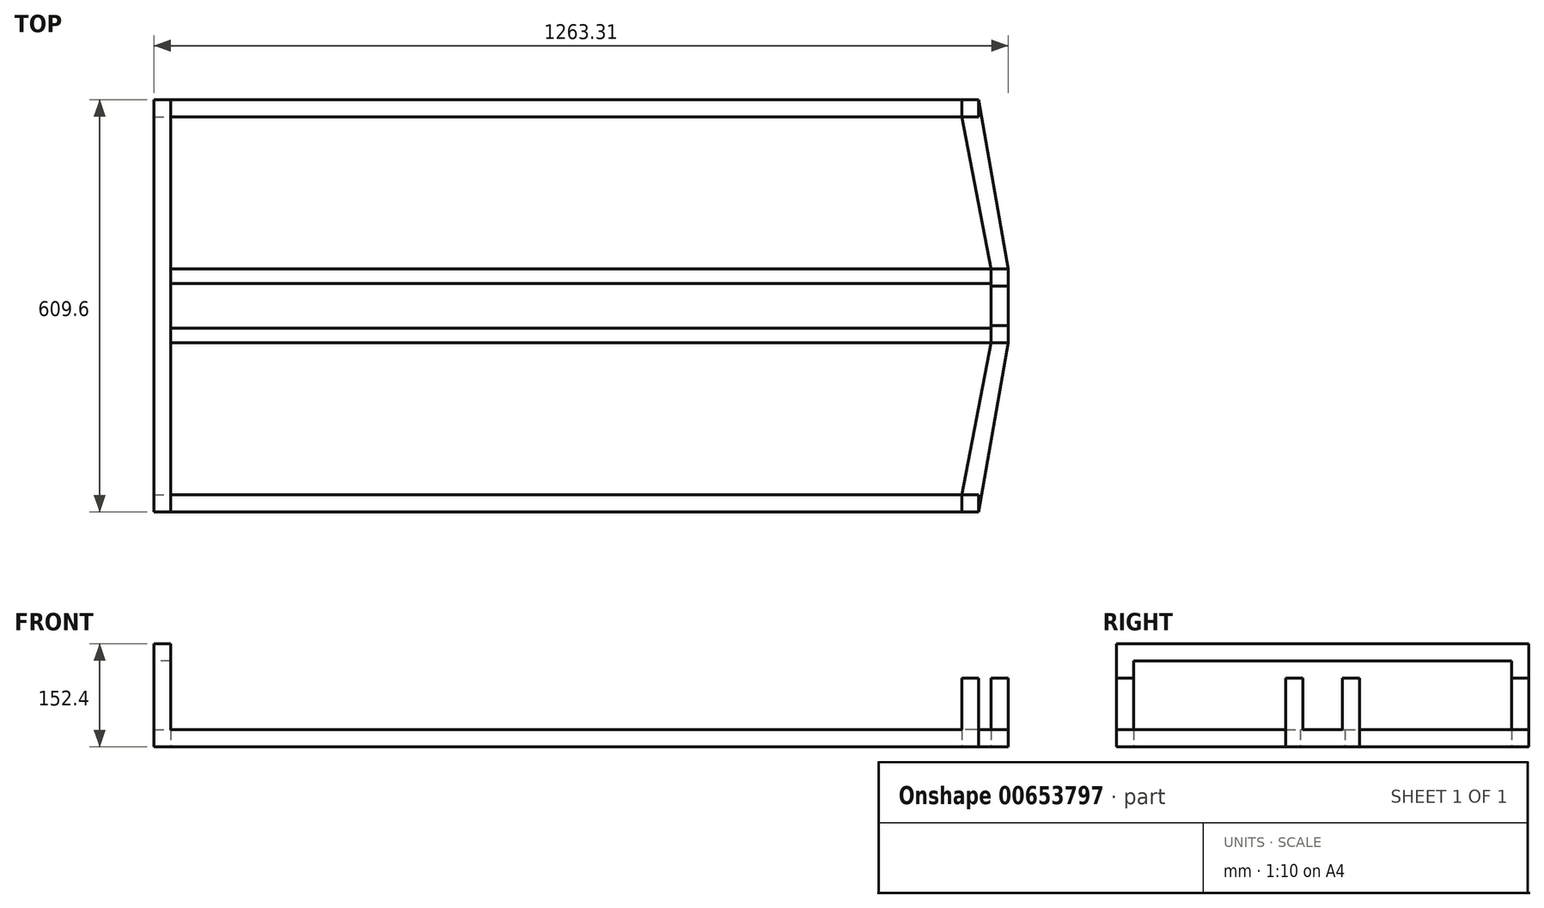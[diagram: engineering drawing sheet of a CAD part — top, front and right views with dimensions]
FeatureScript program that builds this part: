
annotation { "Feature Type Name" : "Feature", "Feature Type Description" : "" }
export const myFeature = defineFeature(function(context is Context, id is Id, definition is map)
    precondition{}
    {
        {
            var Q0;
            Q0=qCreatedBy(makeId("Top.planeOp"),FACE);
            var sketch = newSketch(context, id + "F0", { "sketchPlane" : qUnion([Q0])});
            skLineSegment(sketch, "E0", {"start": v(0, 0) * mm, "end": v(0, 304.8) * mm});
            skLineSegment(sketch, "E1", {"start": v(0, 304.8) * mm, "end": v(1219.2, 304.8) * mm});
            skLineSegment(sketch, "E2", {"start": v(1219.2, 304.8) * mm, "end": v(1263.3, 54.66) * mm});
            skLineSegment(sketch, "E3", {"start": v(1263.3, 54.66) * mm, "end": v(1263.3, 0) * mm});
            skLineSegment(sketch, "E4", {"start": v(1263.3, 0) * mm, "end": v(1237.9, 0) * mm});
            skLineSegment(sketch, "E5", {"start": v(1237.9, 0) * mm, "end": v(1237.9, 54.66) * mm});
            skLineSegment(sketch, "E6", {"start": v(0, 0) * mm, "end": v(25.4, 0) * mm});
            skLineSegment(sketch, "E7", {"start": v(25.4, 0) * mm, "end": v(25.4, 279.4) * mm});
            skLineSegment(sketch, "E8", {"start": v(25.4, 279.4) * mm, "end": v(1194.97, 279.4) * mm});
            skLineSegment(sketch, "E9", {"start": v(1194.97, 279.4) * mm, "end": v(1237.9, 54.66) * mm});
            skLineSegment(sketch, "E10.bottom", {"start": v(1237.9, 54.66) * mm, "end": v(25.4, 54.66) * mm});
            skLineSegment(sketch, "E10.top", {"start": v(1237.9, 33.13) * mm, "end": v(25.4, 33.13) * mm});
            skLineSegment(sketch, "E10.left", {"start": v(1237.9, 54.66) * mm, "end": v(1237.9, 33.13) * mm});
            skLineSegment(sketch, "E10.right", {"start": v(25.4, 54.66) * mm, "end": v(25.4, 33.13) * mm});
            skLineSegment(sketch, "E11.bottom", {"start": v(288.21, 54.66) * mm, "end": v(313.61, 54.66) * mm});
            skLineSegment(sketch, "E11.top", {"start": v(288.21, 279.4) * mm, "end": v(313.61, 279.4) * mm});
            skLineSegment(sketch, "E11.left", {"start": v(288.21, 54.66) * mm, "end": v(288.21, 279.4) * mm});
            skLineSegment(sketch, "E11.right", {"start": v(313.61, 54.66) * mm, "end": v(313.61, 279.4) * mm});
            skLineSegment(sketch, "E12.bottom", {"start": v(697.71, 54.66) * mm, "end": v(723.11, 54.66) * mm});
            skLineSegment(sketch, "E12.top", {"start": v(697.71, 279.4) * mm, "end": v(723.11, 279.4) * mm});
            skLineSegment(sketch, "E12.left", {"start": v(697.71, 54.66) * mm, "end": v(697.71, 279.4) * mm});
            skLineSegment(sketch, "E12.right", {"start": v(723.11, 54.66) * mm, "end": v(723.11, 279.4) * mm});
            skLineSegment(sketch, "E13.bottom", {"start": v(254, 279.4) * mm, "end": v(228.6, 279.4) * mm});
            skLineSegment(sketch, "E13.top", {"start": v(254, 54.66) * mm, "end": v(228.6, 54.66) * mm});
            skLineSegment(sketch, "E13.left", {"start": v(254, 279.4) * mm, "end": v(254, 54.66) * mm});
            skLineSegment(sketch, "E13.right", {"start": v(228.6, 279.4) * mm, "end": v(228.6, 54.66) * mm});
            skSolve(sketch);
        }
        {
            var Q0;
            Q0=makeQuery(id+"F0.imprint","IMPRINT",FACE,{"disambiguationData":[TD([[makeQuery(id+"F0.imprint","IMPRINT",EDGE,{"derivedFrom":sQuery(id+"F0.wireOp",EDGE,"E0")}),-1.0]])]});
            var Q1;
            Q1=makeQuery(id+"F0.imprint","IMPRINT",FACE,{"disambiguationData":[TD([[makeQuery(id+"F0.imprint","IMPRINT",EDGE,{"derivedFrom":sQuery(id+"F0.wireOp",EDGE,"E10.top")}),-1.0]])]});
            var Q2;
            Q2=makeQuery(id+"F0.imprint","IMPRINT",FACE,{"disambiguationData":[TD([[makeQuery(id+"F0.imprint","IMPRINT",EDGE,{"derivedFrom":sQuery(id+"F0.wireOp",EDGE,"E13.bottom")}),1.0]])]});
            var Q3;
            Q3=makeQuery(id+"F0.imprint","IMPRINT",FACE,{"disambiguationData":[TD([[makeQuery(id+"F0.imprint","IMPRINT",EDGE,{"derivedFrom":sQuery(id+"F0.wireOp",EDGE,"E11.bottom")}),1.0]])]});
            var Q4;
            Q4=makeQuery(id+"F0.imprint","IMPRINT",FACE,{"disambiguationData":[TD([[makeQuery(id+"F0.imprint","IMPRINT",EDGE,{"derivedFrom":sQuery(id+"F0.wireOp",EDGE,"E12.bottom")}),1.0]])]});
            extrude(context, id + "F1", {"entities" : qUnion([Q0, Q1, Q2, Q3, Q4]), "depth" : 25.4 * mm, "offsetDistance" : 25.4 * mm});
        }
        {
            var Q0;
            Q0=makeQuery(id+"F1.opExtrude","SWEPT_BODY",BODY,{"disambiguationData":[OSD([sQuery(id+"F0.wireOp",EDGE,"E0"),sQuery(id+"F0.wireOp",EDGE,"E1"),sQuery(id+"F0.wireOp",EDGE,"E2"),sQuery(id+"F0.wireOp",EDGE,"E3"),sQuery(id+"F0.wireOp",EDGE,"E4"),sQuery(id+"F0.wireOp",EDGE,"E5"),sQuery(id+"F0.wireOp",EDGE,"E6"),sQuery(id+"F0.wireOp",EDGE,"E7"),sQuery(id+"F0.wireOp",EDGE,"E8"),sQuery(id+"F0.wireOp",EDGE,"E9"),sQuery(id+"F0.wireOp",EDGE,"E10.bottom"),sQuery(id+"F0.wireOp",EDGE,"E10.top"),sQuery(id+"F0.wireOp",EDGE,"E11.left"),sQuery(id+"F0.wireOp",EDGE,"E11.right"),sQuery(id+"F0.wireOp",EDGE,"E12.left"),sQuery(id+"F0.wireOp",EDGE,"E12.right"),sQuery(id+"F0.wireOp",EDGE,"E13.left"),sQuery(id+"F0.wireOp",EDGE,"E13.right")])]});
            var Q1;
            Q1=qCreatedBy(makeId("Front.planeOp"),FACE);
            mirror(context, id + "F2", {"operationType" : NewBodyOperationType.ADD, "entities" : qUnion([Q0]), "mirrorPlane" : qUnion([Q1])});
        }
        {
            var Q0;
            {var subQ0=makeQuery(id+"F1.opExtrude","CAP_FACE",FACE,{"disambiguationData":[OSD([sQuery(id+"F0.wireOp",EDGE,"E0"),sQuery(id+"F0.wireOp",EDGE,"E1"),sQuery(id+"F0.wireOp",EDGE,"E2"),sQuery(id+"F0.wireOp",EDGE,"E3"),sQuery(id+"F0.wireOp",EDGE,"E4"),sQuery(id+"F0.wireOp",EDGE,"E5"),sQuery(id+"F0.wireOp",EDGE,"E6"),sQuery(id+"F0.wireOp",EDGE,"E7"),sQuery(id+"F0.wireOp",EDGE,"E8"),sQuery(id+"F0.wireOp",EDGE,"E9"),sQuery(id+"F0.wireOp",EDGE,"E10.bottom"),sQuery(id+"F0.wireOp",EDGE,"E10.top"),sQuery(id+"F0.wireOp",EDGE,"E11.left"),sQuery(id+"F0.wireOp",EDGE,"E11.right"),sQuery(id+"F0.wireOp",EDGE,"E12.left"),sQuery(id+"F0.wireOp",EDGE,"E12.right"),sQuery(id+"F0.wireOp",EDGE,"E13.left"),sQuery(id+"F0.wireOp",EDGE,"E13.right")])],"isStart":false});Q0=makeQuery(id+"F2.boolean.opBoolean","MERGE",FACE,{"derivedFrom":[subQ0,makeQuery(id+"F2.opPattern","COPY",FACE,{"derivedFrom":subQ0,"instanceName":"1"})]});}
            var sketch = newSketch(context, id + "F3", { "sketchPlane" : qUnion([Q0])});
            skLineSegment(sketch, "E14.bottom", {"start": v(1219.2, -304.8) * mm, "end": v(1194.97, -304.8) * mm});
            skLineSegment(sketch, "E14.top", {"start": v(1219.2, -279.4) * mm, "end": v(1194.97, -279.4) * mm});
            skLineSegment(sketch, "E14.left", {"start": v(1219.2, -304.8) * mm, "end": v(1219.2, -279.4) * mm});
            skLineSegment(sketch, "E14.right", {"start": v(1194.97, -304.8) * mm, "end": v(1194.97, -279.4) * mm});
            skLineSegment(sketch, "E15.bottom", {"start": v(25.4, -279.4) * mm, "end": v(0, -279.4) * mm});
            skLineSegment(sketch, "E15.top", {"start": v(25.4, -304.8) * mm, "end": v(0, -304.8) * mm});
            skLineSegment(sketch, "E15.left", {"start": v(25.4, -279.4) * mm, "end": v(25.4, -304.8) * mm});
            skLineSegment(sketch, "E15.right", {"start": v(0, -279.4) * mm, "end": v(0, -304.8) * mm});
            skLineSegment(sketch, "E16.bottom", {"start": v(723.11, -279.4) * mm, "end": v(697.71, -279.4) * mm});
            skLineSegment(sketch, "E16.top", {"start": v(723.11, -304.8) * mm, "end": v(697.71, -304.8) * mm});
            skLineSegment(sketch, "E16.left", {"start": v(723.11, -279.4) * mm, "end": v(723.11, -304.8) * mm});
            skLineSegment(sketch, "E16.right", {"start": v(697.71, -279.4) * mm, "end": v(697.71, -304.8) * mm});
            skLineSegment(sketch, "E17.bottom", {"start": v(1219.2, 304.8) * mm, "end": v(1194.97, 304.8) * mm});
            skLineSegment(sketch, "E17.top", {"start": v(1219.2, 279.4) * mm, "end": v(1194.97, 279.4) * mm});
            skLineSegment(sketch, "E17.left", {"start": v(1219.2, 304.8) * mm, "end": v(1219.2, 279.4) * mm});
            skLineSegment(sketch, "E17.right", {"start": v(1194.97, 304.8) * mm, "end": v(1194.97, 279.4) * mm});
            skLineSegment(sketch, "E18.bottom", {"start": v(723.11, 279.4) * mm, "end": v(697.71, 279.4) * mm});
            skLineSegment(sketch, "E18.top", {"start": v(723.11, 304.8) * mm, "end": v(697.71, 304.8) * mm});
            skLineSegment(sketch, "E18.left", {"start": v(723.11, 279.4) * mm, "end": v(723.11, 304.8) * mm});
            skLineSegment(sketch, "E18.right", {"start": v(697.71, 279.4) * mm, "end": v(697.71, 304.8) * mm});
            skLineSegment(sketch, "E19.bottom", {"start": v(25.4, 279.4) * mm, "end": v(0, 279.4) * mm});
            skLineSegment(sketch, "E19.top", {"start": v(25.4, 304.8) * mm, "end": v(0, 304.8) * mm});
            skLineSegment(sketch, "E19.left", {"start": v(25.4, 279.4) * mm, "end": v(25.4, 304.8) * mm});
            skLineSegment(sketch, "E19.right", {"start": v(0, 279.4) * mm, "end": v(0, 304.8) * mm});
            skLineSegment(sketch, "E20.bottom", {"start": v(1237.9, -54.66) * mm, "end": v(1263.3, -54.66) * mm});
            skLineSegment(sketch, "E20.top", {"start": v(1237.9, -29.26) * mm, "end": v(1263.3, -29.26) * mm});
            skLineSegment(sketch, "E20.left", {"start": v(1237.9, -54.66) * mm, "end": v(1237.9, -29.26) * mm});
            skLineSegment(sketch, "E20.right", {"start": v(1263.3, -54.66) * mm, "end": v(1263.3, -29.26) * mm});
            skLineSegment(sketch, "E21.bottom", {"start": v(1237.9, 54.66) * mm, "end": v(1263.3, 54.66) * mm});
            skLineSegment(sketch, "E21.top", {"start": v(1237.9, 29.26) * mm, "end": v(1263.3, 29.26) * mm});
            skLineSegment(sketch, "E21.left", {"start": v(1237.9, 54.66) * mm, "end": v(1237.9, 29.26) * mm});
            skLineSegment(sketch, "E21.right", {"start": v(1263.3, 54.66) * mm, "end": v(1263.3, 29.26) * mm});
            skSolve(sketch);
        }
        {
            var Q0;
            Q0=makeQuery(id+"F3.imprint","IMPRINT",FACE,{"disambiguationData":[TD([[makeQuery(id+"F3.imprint","IMPRINT",EDGE,{"derivedFrom":sQuery(id+"F3.wireOp",EDGE,"E14.bottom")}),1.0]])]});
            var Q1;
            {var subQ2=sQuery(id+"F3.wireOp",EDGE,"E20.bottom");Q1=makeQuery(id+"F3.imprint","IMPRINT",FACE,{"disambiguationData":[TD([[makeQuery(id+"F3.imprint","IMPRINT",EDGE,{"derivedFrom":subQ2}),1.0]])]});}
            var Q2;
            {var subQ4=sQuery(id+"F3.wireOp",EDGE,"E21.bottom");Q2=makeQuery(id+"F3.imprint","IMPRINT",FACE,{"disambiguationData":[TD([[makeQuery(id+"F3.imprint","IMPRINT",EDGE,{"derivedFrom":subQ4}),-1.0]])]});}
            var Q3;
            Q3=makeQuery(id+"F3.imprint","IMPRINT",FACE,{"disambiguationData":[TD([[makeQuery(id+"F3.imprint","IMPRINT",EDGE,{"derivedFrom":sQuery(id+"F3.wireOp",EDGE,"E17.bottom")}),-1.0]])]});
            extrude(context, id + "F4", {"entities" : qUnion([Q0, Q1, Q2, Q3]), "operationType" : NewBodyOperationType.ADD, "depth" : 76.2 * mm, "offsetDistance" : 25.4 * mm});
        }
        {
            var Q0;
            {var subQ0=sQuery(id+"F0.wireOp",EDGE,"E12.right");var subQ2=sQuery(id+"F0.wireOp",EDGE,"E13.right");var subQ4=sQuery(id+"F0.wireOp",EDGE,"E12.left");var subQ6=sQuery(id+"F0.wireOp",EDGE,"E11.left");var subQ8=sQuery(id+"F0.wireOp",EDGE,"E10.top");var subQ11=sQuery(id+"F0.wireOp",EDGE,"E10.bottom");var subQ12=sQuery(id+"F0.wireOp",EDGE,"E7");var subQ16=sQuery(id+"F0.wireOp",EDGE,"E13.left");var subQ20=sQuery(id+"F0.wireOp",EDGE,"E11.right");var subQ23=sQuery(id+"F0.wireOp",EDGE,"E9");var subQ27=sQuery(id+"F0.wireOp",EDGE,"E8");var subQ37=sQuery(id+"F0.wireOp",EDGE,"E6");var subQ39=sQuery(id+"F0.wireOp",EDGE,"E5");var subQ41=sQuery(id+"F0.wireOp",EDGE,"E1");var subQ43=sQuery(id+"F0.wireOp",EDGE,"E0");var subQ44=makeQuery(id+"F1.opExtrude","CAP_FACE",FACE,{"disambiguationData":[OSD([subQ43,subQ41,sQuery(id+"F0.wireOp",EDGE,"E2"),sQuery(id+"F0.wireOp",EDGE,"E3"),sQuery(id+"F0.wireOp",EDGE,"E4"),subQ39,subQ37,subQ12,subQ27,subQ23,subQ11,subQ8,subQ6,subQ20,subQ4,subQ0,subQ16,subQ2])],"isStart":false});var subQ45=makeQuery(id+"F2.opPattern","COPY",FACE,{"derivedFrom":subQ44,"instanceName":"1"});var subQ46=makeQuery(id+"F1.opExtrude","SWEPT_FACE",FACE,{"disambiguationData":[OSD([subQ43])]});Q0=makeQuery(id+"F4.boolean.opBoolean","SPLIT",FACE,{"disambiguationData":[TD([subQ46])],"derivedFrom":makeQuery(id+"F2.boolean.opBoolean","MERGE",FACE,{"derivedFrom":[subQ44,subQ45]})});}
            var sketch = newSketch(context, id + "F5", { "sketchPlane" : qUnion([Q0])});
            skLineSegment(sketch, "E22.bottom", {"start": v(0, 304.8) * mm, "end": v(25.4, 304.8) * mm});
            skLineSegment(sketch, "E22.top", {"start": v(0, 279.4) * mm, "end": v(25.4, 279.4) * mm});
            skLineSegment(sketch, "E22.left", {"start": v(0, 304.8) * mm, "end": v(0, 279.4) * mm});
            skLineSegment(sketch, "E22.right", {"start": v(25.4, 304.8) * mm, "end": v(25.4, 279.4) * mm});
            skLineSegment(sketch, "E23.bottom", {"start": v(0, -304.8) * mm, "end": v(25.4, -304.8) * mm});
            skLineSegment(sketch, "E23.top", {"start": v(0, -279.4) * mm, "end": v(25.4, -279.4) * mm});
            skLineSegment(sketch, "E23.left", {"start": v(0, -304.8) * mm, "end": v(0, -279.4) * mm});
            skLineSegment(sketch, "E23.right", {"start": v(25.4, -304.8) * mm, "end": v(25.4, -279.4) * mm});
            skSolve(sketch);
        }
        {
            var Q0;
            Q0=makeQuery(id+"F5.imprint","IMPRINT",FACE,{"disambiguationData":[TD([[makeQuery(id+"F5.imprint","IMPRINT",EDGE,{"derivedFrom":sQuery(id+"F5.wireOp",EDGE,"E22.bottom")}),-1.0]])]});
            var Q1;
            Q1=makeQuery(id+"F5.imprint","IMPRINT",FACE,{"disambiguationData":[TD([[makeQuery(id+"F5.imprint","IMPRINT",EDGE,{"derivedFrom":sQuery(id+"F5.wireOp",EDGE,"E23.bottom")}),1.0]])]});
            extrude(context, id + "F6", {"entities" : qUnion([Q0, Q1]), "operationType" : NewBodyOperationType.ADD, "depth" : 127 * mm, "offsetDistance" : 25.4 * mm});
        }
        {
            var Q0;
            Q0=makeQuery(id+"F6.opExtrude","SWEPT_FACE",FACE,{"disambiguationData":[OSD([sQuery(id+"F5.wireOp",EDGE,"E22.top")])]});
            var sketch = newSketch(context, id + "F7", { "sketchPlane" : qUnion([Q0])});
            skLineSegment(sketch, "E24.bottom", {"start": v(25.4, 152.4) * mm, "end": v(0, 152.4) * mm});
            skLineSegment(sketch, "E24.top", {"start": v(25.4, 127) * mm, "end": v(0, 127) * mm});
            skLineSegment(sketch, "E24.left", {"start": v(25.4, 152.4) * mm, "end": v(25.4, 127) * mm});
            skLineSegment(sketch, "E24.right", {"start": v(0, 152.4) * mm, "end": v(0, 127) * mm});
            skSolve(sketch);
        }
        {
            var Q0;
            Q0=makeQuery(id+"F7.imprint","IMPRINT",FACE,{"disambiguationData":[TD([[makeQuery(id+"F7.imprint","IMPRINT",EDGE,{"derivedFrom":sQuery(id+"F7.wireOp",EDGE,"E24.bottom")}),-1.0]])]});
            extrude(context, id + "F8", {"entities" : qUnion([Q0]), "operationType" : NewBodyOperationType.ADD, "depth" : 573.02 * mm, "offsetDistance" : 25.4 * mm});
        }
    });
